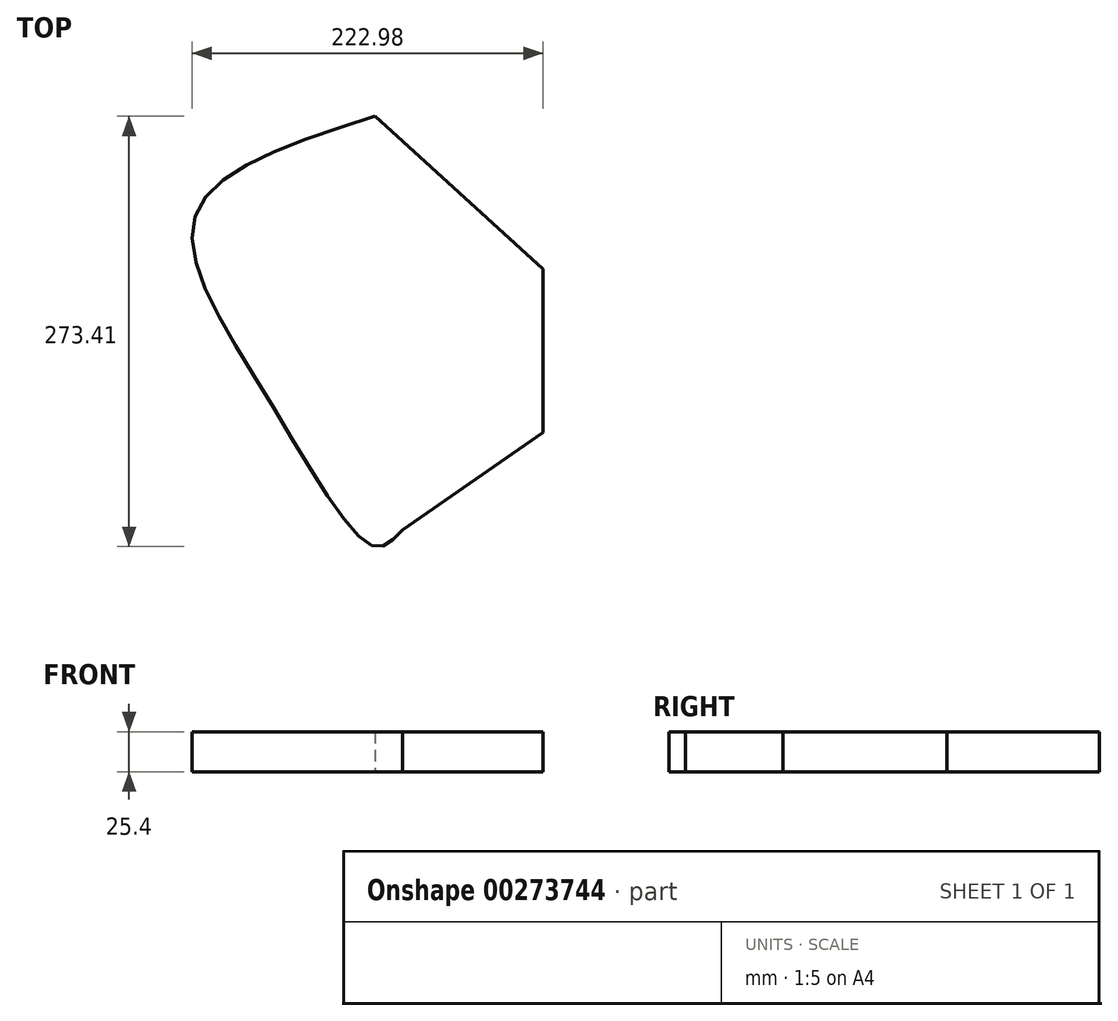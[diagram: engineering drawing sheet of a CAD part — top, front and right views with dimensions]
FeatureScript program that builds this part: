
annotation { "Feature Type Name" : "Feature", "Feature Type Description" : "" }
export const myFeature = defineFeature(function(context is Context, id is Id, definition is map)
    precondition{}
    {
        {
            var Q0;
            Q0=qCreatedBy(makeId("Top.planeOp"),FACE);
            var sketch = newSketch(context, id + "F0", { "sketchPlane" : qUnion([Q0])});
            skLineSegment(sketch, "E0", {"start": v(40.53, -122.8) * mm, "end": v(129.89, -60.91) * mm});
            skLineSegment(sketch, "E1", {"start": v(129.89, -60.91) * mm, "end": v(129.89, 43.04) * mm});
            skLineSegment(sketch, "E2", {"start": v(129.89, 43.04) * mm, "end": v(23.15, 140) * mm});
            skFitSpline(sketch, "E3", {"points": [v(23.15, 140) * mm, v(-90.92, 77.23) * mm, v(-44.34, -40.01) * mm, v(23.15, -133.16) * mm, v(40.53, -122.8) * mm], "startDerivative": vector(-514.96, -163.76) * mm, "endDerivative": vector(133.5, 150.1) * mm});
            skSolve(sketch);
        }
        {
            var Q0;
            Q0=makeQuery(id+"F0.imprint","IMPRINT",FACE,{"disambiguationData":[TD([[makeQuery(id+"F0.imprint","IMPRINT",EDGE,{"derivedFrom":sQuery(id+"F0.wireOp",EDGE,"E0")}),1.0]])]});
            extrude(context, id + "F1", {"entities" : qUnion([Q0]), "depth" : 25.4 * mm});
        }
    });
